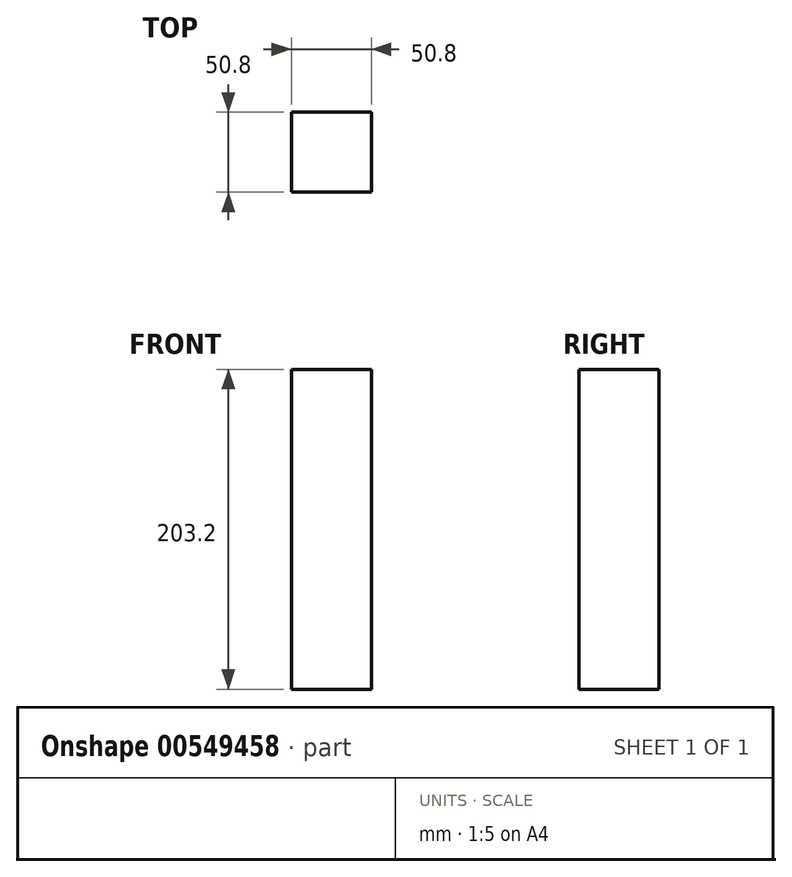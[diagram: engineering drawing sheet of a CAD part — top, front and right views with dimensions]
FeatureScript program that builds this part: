
annotation { "Feature Type Name" : "Feature", "Feature Type Description" : "" }
export const myFeature = defineFeature(function(context is Context, id is Id, definition is map)
    precondition{}
    {
        {
            var Q0;
            Q0=qCreatedBy(makeId("Top.planeOp"),FACE);
            var sketch = newSketch(context, id + "F0", { "sketchPlane" : qUnion([Q0])});
            skLineSegment(sketch, "E0.bottom", {"start": v(-25.4, 25.4) * mm, "end": v(25.4, 25.4) * mm});
            skLineSegment(sketch, "E0.top", {"start": v(-25.4, -25.4) * mm, "end": v(25.4, -25.4) * mm});
            skLineSegment(sketch, "E0.left", {"start": v(-25.4, 25.4) * mm, "end": v(-25.4, -25.4) * mm});
            skLineSegment(sketch, "E0.right", {"start": v(25.4, 25.4) * mm, "end": v(25.4, -25.4) * mm});
            skPoint(sketch, "E0.middle", {"position": v(0, 0) * mm});
            skSolve(sketch);
        }
        {
            var Q0;
            Q0=makeQuery(id+"F0.imprint","IMPRINT",FACE,{"disambiguationData":[TD([[makeQuery(id+"F0.imprint","IMPRINT",EDGE,{"derivedFrom":sQuery(id+"F0.wireOp",EDGE,"E0.bottom")}),-1.0]])]});
            extrude(context, id + "F1", {"entities" : qUnion([Q0]), "depth" : 203.2 * mm, "offsetDistance" : 25.4 * mm});
        }
    });
